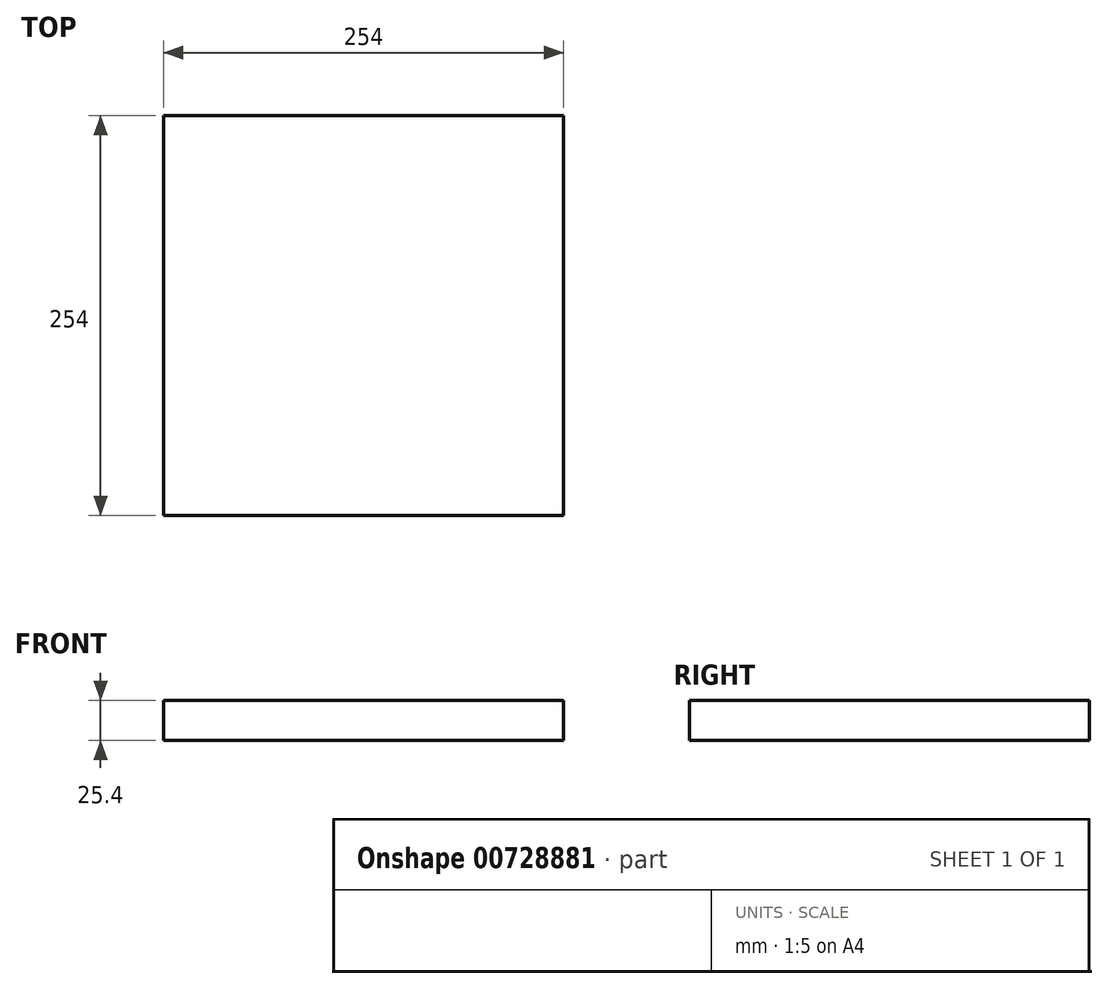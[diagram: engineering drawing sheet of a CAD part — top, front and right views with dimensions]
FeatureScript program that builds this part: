
annotation { "Feature Type Name" : "Feature", "Feature Type Description" : "" }
export const myFeature = defineFeature(function(context is Context, id is Id, definition is map)
    precondition{}
    {
        {
            var Q0;
            Q0=qCreatedBy(makeId("Top.planeOp"),FACE);
            cPlane(context, id + "F0", {"entities" : qUnion([Q0]), "cplaneType" : CPlaneType.OFFSET, "offset" : 1244.6 * mm, "oppositeDirection" : true, "width" : 152.4 * mm, "height" : 152.4 * mm});
        }
        {
            var Q0;
            Q0=qCreatedBy(id+"F0.planeOp",FACE);
            var sketch = newSketch(context, id + "F1", { "sketchPlane" : qUnion([Q0])});
            skLineSegment(sketch, "E0.bottom", {"start": v(127, -127) * mm, "end": v(-127, -127) * mm});
            skLineSegment(sketch, "E0.top", {"start": v(127, 127) * mm, "end": v(-127, 127) * mm});
            skLineSegment(sketch, "E0.left", {"start": v(127, -127) * mm, "end": v(127, 127) * mm});
            skLineSegment(sketch, "E0.right", {"start": v(-127, -127) * mm, "end": v(-127, 127) * mm});
            skPoint(sketch, "E0.middle", {"position": v(0, 0) * mm});
            skSolve(sketch);
        }
        {
            var Q0;
            Q0=makeQuery(id+"F1.imprint","IMPRINT",FACE,{"disambiguationData":[TD([[makeQuery(id+"F1.imprint","IMPRINT",EDGE,{"derivedFrom":sQuery(id+"F1.wireOp",EDGE,"E0.bottom")}),-1.0]])]});
            extrude(context, id + "F2", {"entities" : qUnion([Q0]), "depth" : 25.4 * mm, "offsetDistance" : 25.4 * mm});
        }
        {
            var Q0;
            Q0=makeQuery(id+"F2.opExtrude","CAP_FACE",FACE,{"disambiguationData":[OSD([sQuery(id+"F1.wireOp",EDGE,"E0.bottom"),sQuery(id+"F1.wireOp",EDGE,"E0.top"),sQuery(id+"F1.wireOp",EDGE,"E0.left"),sQuery(id+"F1.wireOp",EDGE,"E0.right")])],"isStart":false});
            cPlane(context, id + "F3", {"entities" : qUnion([Q0]), "cplaneType" : CPlaneType.OFFSET, "offset" : 1524 * mm, "width" : 152.4 * mm, "height" : 152.4 * mm});
        }
        {
            var Q0;
            Q0=qCreatedBy(id+"F3.planeOp",FACE);
            var sketch = newSketch(context, id + "F4", { "sketchPlane" : qUnion([Q0])});
            skLineSegment(sketch, "E1.bottom", {"start": v(177.8, -177.8) * mm, "end": v(-177.8, -177.8) * mm});
            skLineSegment(sketch, "E1.top", {"start": v(177.8, 177.8) * mm, "end": v(-177.8, 177.8) * mm});
            skLineSegment(sketch, "E1.left", {"start": v(177.8, -177.8) * mm, "end": v(177.8, 177.8) * mm});
            skLineSegment(sketch, "E1.right", {"start": v(-177.8, -177.8) * mm, "end": v(-177.8, 177.8) * mm});
            skPoint(sketch, "E1.middle", {"position": v(0, 0) * mm});
            skSolve(sketch);
        }
        {
            var Q0;
            Q0=makeQuery(id+"F2.opExtrude","CAP_FACE",FACE,{"disambiguationData":[OSD([sQuery(id+"F1.wireOp",EDGE,"E0.bottom"),sQuery(id+"F1.wireOp",EDGE,"E0.top"),sQuery(id+"F1.wireOp",EDGE,"E0.left"),sQuery(id+"F1.wireOp",EDGE,"E0.right")])],"isStart":false});
            cPlane(context, id + "F5", {"entities" : qUnion([Q0]), "cplaneType" : CPlaneType.OFFSET, "offset" : 2.54 * mm, "width" : 152.4 * mm, "height" : 152.4 * mm});
        }
        {
            var Q0;
            Q0=qCreatedBy(id+"F5.planeOp",FACE);
            var sketch = newSketch(context, id + "F6", { "sketchPlane" : qUnion([Q0])});
            skPoint(sketch, "E2", {"position": v(0, 0) * mm});
            skSolve(sketch);
        }
        {
            var Q0;
            Q0=sQuery(id+"F4.wireOp",VERTEX,"E1.left.end");
            var Q1;
            Q1=sQuery(id+"F4.wireOp",VERTEX,"E1.left.start");
            var Q2;
            Q2=sQuery(id+"F6.wireOp",VERTEX,"E2");
            cPlane(context, id + "F7", {"entities" : qUnion([Q0, Q1, Q2]), "cplaneType" : CPlaneType.THREE_POINT, "offset" : 25.4 * mm, "width" : 152.4 * mm, "height" : 152.4 * mm});
        }
    });
